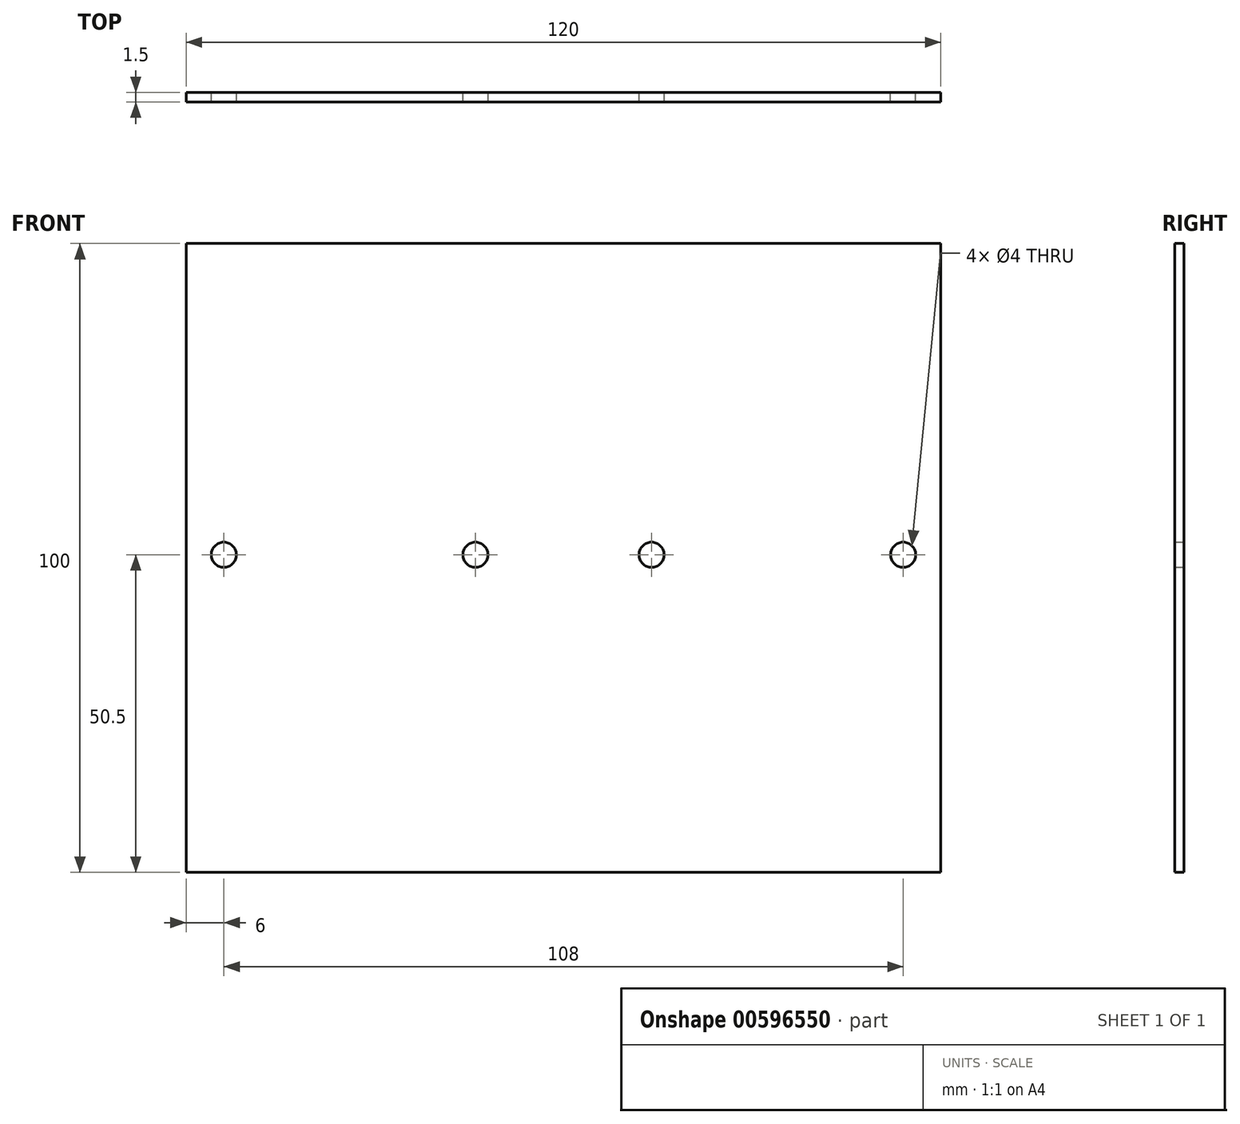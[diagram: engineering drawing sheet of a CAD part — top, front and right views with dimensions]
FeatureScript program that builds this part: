
annotation { "Feature Type Name" : "Feature", "Feature Type Description" : "" }
export const myFeature = defineFeature(function(context is Context, id is Id, definition is map)
    precondition{}
    {
        {
            var Q0;
            Q0=qCreatedBy(makeId("Front.planeOp"),FACE);
            var sketch = newSketch(context, id + "F0", { "sketchPlane" : qUnion([Q0])});
            skLineSegment(sketch, "E0.bottom", {"start": v(0, 0) * mm, "end": v(120, 0) * mm});
            skLineSegment(sketch, "E0.top", {"start": v(0, 100) * mm, "end": v(120, 100) * mm});
            skLineSegment(sketch, "E0.left", {"start": v(0, 0) * mm, "end": v(0, 100) * mm});
            skLineSegment(sketch, "E0.right", {"start": v(120, 0) * mm, "end": v(120, 100) * mm});
            skCircle(sketch, "E1", {"center": v(114, 50.5) * mm, "radius": 2 * mm});
            skCircle(sketch, "E2", {"center": v(74, 50.5) * mm, "radius": 2 * mm});
            skCircle(sketch, "E3", {"center": v(46, 50.5) * mm, "radius": 2 * mm});
            skCircle(sketch, "E4", {"center": v(6, 50.5) * mm, "radius": 2 * mm});
            skSolve(sketch);
        }
        {
            var Q0;
            Q0=makeQuery(id+"F0.imprint","IMPRINT",FACE,{"disambiguationData":[TD([[makeQuery(id+"F0.imprint","IMPRINT",EDGE,{"derivedFrom":sQuery(id+"F0.wireOp",EDGE,"E0.bottom")}),1.0]])]});
            extrude(context, id + "F1", {"entities" : qUnion([Q0]), "depth" : 1.5 * mm, "offsetDistance" : 25 * mm});
        }
    });
